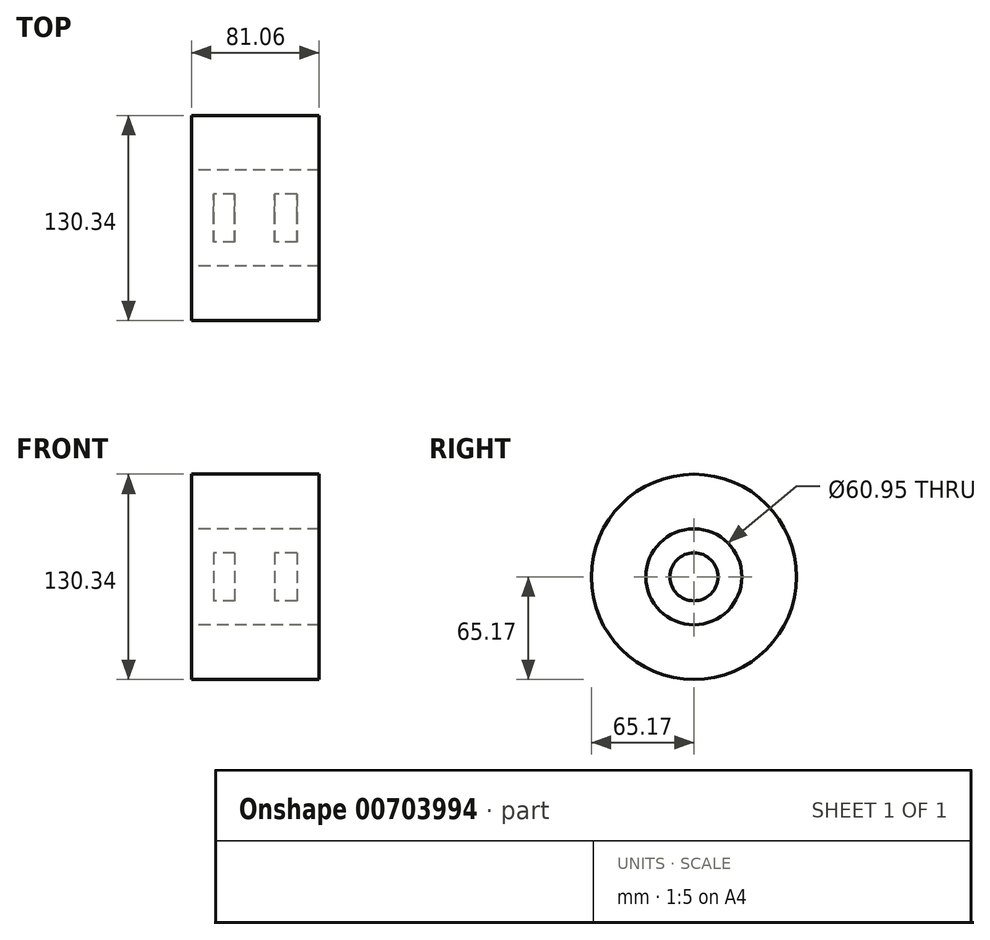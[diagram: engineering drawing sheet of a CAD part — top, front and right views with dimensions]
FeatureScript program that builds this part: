
annotation { "Feature Type Name" : "Feature", "Feature Type Description" : "" }
export const myFeature = defineFeature(function(context is Context, id is Id, definition is map)
    precondition{}
    {
        {
            var Q0;
            Q0=qCreatedBy(makeId("Front.planeOp"),FACE);
            var sketch = newSketch(context, id + "F0", { "sketchPlane" : qUnion([Q0])});
            skLineSegment(sketch, "E0.bottom", {"start": v(-40.55, 65.17) * mm, "end": v(40.5, 65.17) * mm});
            skLineSegment(sketch, "E0.top", {"start": v(-40.55, 30.48) * mm, "end": v(40.5, 30.48) * mm});
            skLineSegment(sketch, "E0.left", {"start": v(-40.55, 65.17) * mm, "end": v(-40.55, 30.48) * mm});
            skLineSegment(sketch, "E0.right", {"start": v(40.5, 65.17) * mm, "end": v(40.5, 30.48) * mm});
            skLineSegment(sketch, "E1.bottom", {"start": v(-13.13, 30.48) * mm, "end": v(12.1, 30.48) * mm});
            skLineSegment(sketch, "E1.top", {"start": v(-13.13, 0) * mm, "end": v(12.1, 0) * mm});
            skLineSegment(sketch, "E1.left", {"start": v(-13.13, 30.48) * mm, "end": v(-13.13, 0) * mm});
            skLineSegment(sketch, "E1.right", {"start": v(12.1, 30.48) * mm, "end": v(12.1, 0) * mm});
            skLineSegment(sketch, "E2.bottom", {"start": v(-13.13, 15.24) * mm, "end": v(-26.47, 15.24) * mm});
            skLineSegment(sketch, "E2.top", {"start": v(-13.13, 0) * mm, "end": v(-26.47, 0) * mm});
            skLineSegment(sketch, "E2.left", {"start": v(-13.13, 15.24) * mm, "end": v(-13.13, 0) * mm});
            skLineSegment(sketch, "E2.right", {"start": v(-26.47, 15.24) * mm, "end": v(-26.47, 0) * mm});
            skLineSegment(sketch, "E3.bottom", {"start": v(12.1, 15.24) * mm, "end": v(26.4, 15.24) * mm});
            skLineSegment(sketch, "E3.top", {"start": v(12.1, 0) * mm, "end": v(26.4, 0) * mm});
            skLineSegment(sketch, "E3.left", {"start": v(12.1, 15.24) * mm, "end": v(12.1, 0) * mm});
            skLineSegment(sketch, "E3.right", {"start": v(26.4, 15.24) * mm, "end": v(26.4, 0) * mm});
            skSolve(sketch);
        }
        {
            var Q0;
            Q0=makeQuery(id+"F0.imprint","IMPRINT",FACE,{"disambiguationData":[TD([[makeQuery(id+"F0.imprint","IMPRINT",EDGE,{"derivedFrom":sQuery(id+"F0.wireOp",EDGE,"E3.bottom")}),-1.0]])]});
            var Q1;
            Q1=makeQuery(id+"F0.imprint","IMPRINT",FACE,{"disambiguationData":[TD([[makeQuery(id+"F0.imprint","IMPRINT",EDGE,{"derivedFrom":sQuery(id+"F0.wireOp",EDGE,"E1.bottom")}),-1.0]])]});
            var Q2;
            Q2=makeQuery(id+"F0.imprint","IMPRINT",FACE,{"disambiguationData":[TD([[makeQuery(id+"F0.imprint","IMPRINT",EDGE,{"derivedFrom":sQuery(id+"F0.wireOp",EDGE,"E2.bottom")}),1.0]])]});
            var Q3;
            Q3=makeQuery(id+"F0.imprint","IMPRINT",FACE,{"disambiguationData":[TD([[makeQuery(id+"F0.imprint","IMPRINT",EDGE,{"derivedFrom":sQuery(id+"F0.wireOp",EDGE,"E0.bottom")}),-1.0]])]});
            var Q4;
            Q4=sQuery(id+"F0.wireOp",EDGE,"E1.top");
            revolve(context, id + "F1", {"surfaceOperationType" : NewSurfaceOperationType.NEW, "entities" : qUnion([Q0, Q1, Q2, Q3]), "axis" : qUnion([Q4]), "revolveType" : RevolveType.FULL});
        }
    });
